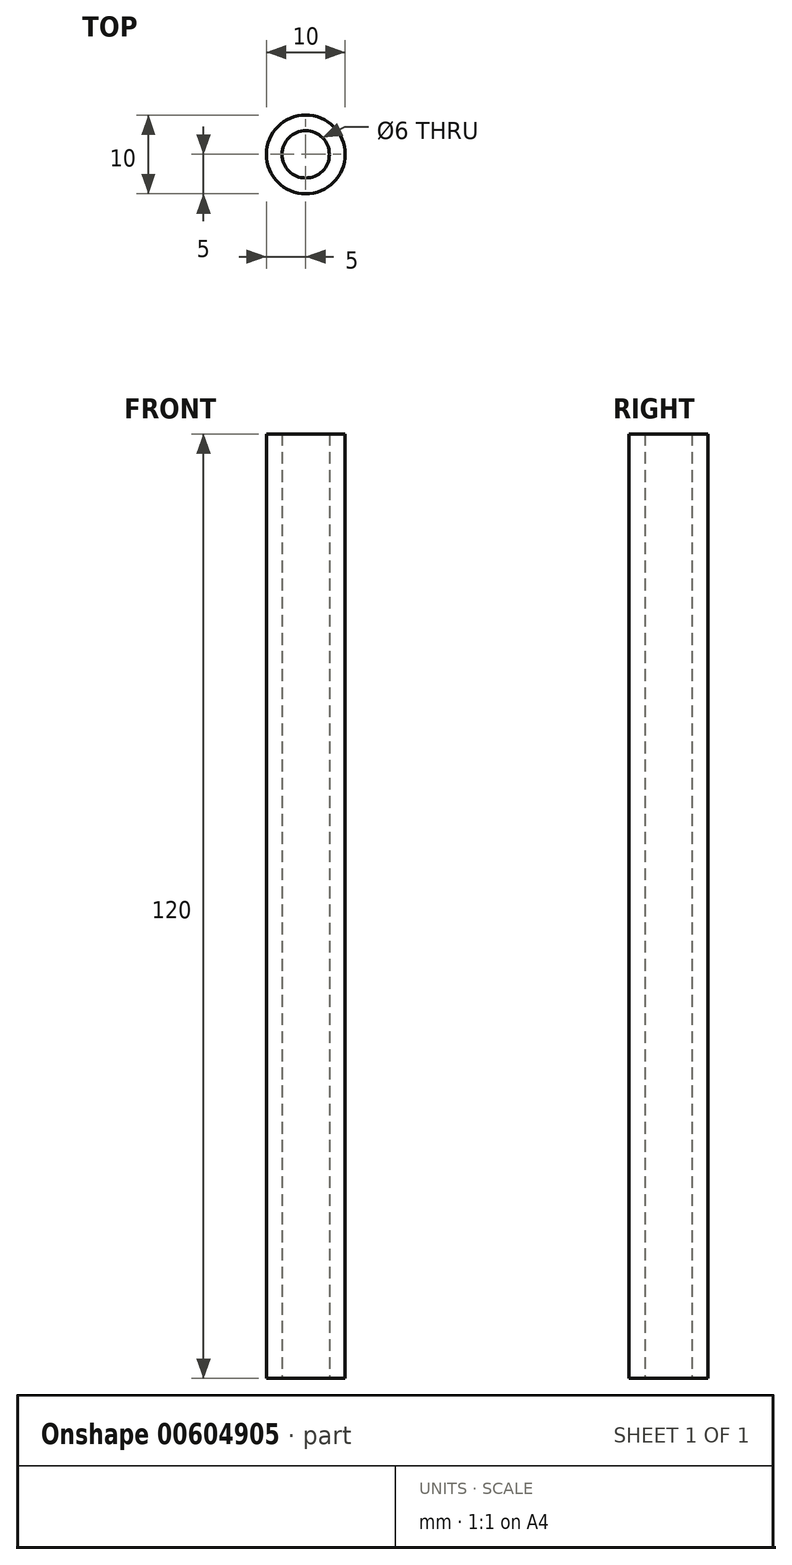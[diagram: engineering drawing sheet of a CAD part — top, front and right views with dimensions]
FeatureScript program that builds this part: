
annotation { "Feature Type Name" : "Feature", "Feature Type Description" : "" }
export const myFeature = defineFeature(function(context is Context, id is Id, definition is map)
    precondition{}
    {
        {
            var Q0;
            Q0=qCreatedBy(makeId("Top.planeOp"),FACE);
            var sketch = newSketch(context, id + "F0", { "sketchPlane" : qUnion([Q0])});
            skCircle(sketch, "E0", {"center": v(0, 0) * mm, "radius": 3 * mm});
            skCircle(sketch, "E1", {"center": v(0, 0) * mm, "radius": 5 * mm});
            skSolve(sketch);
        }
        {
            var Q0;
            Q0=makeQuery(id+"F0.imprint","IMPRINT",FACE,{"disambiguationData":[TD([[makeQuery(id+"F0.imprint","IMPRINT",EDGE,{"derivedFrom":sQuery(id+"F0.wireOp",EDGE,"E0")}),-1.0]])]});
            extrude(context, id + "F1", {"entities" : qUnion([Q0]), "depth" : 120 * mm, "offsetDistance" : 25 * mm});
        }
    });
